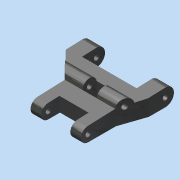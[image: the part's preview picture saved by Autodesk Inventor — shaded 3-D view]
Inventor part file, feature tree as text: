
AUTODESK INVENTOR PART (.ipt)
format: ipt  version: 2014 (Build 180170000, 170)  size: 160,256 bytes
history: native  units: in
note: dims shown in document units (in); Inventor stores cm internally (conversion verified against a paired STEP export)
features: other x3, plane x3, sketch x2
ambient origin geometry x8: Origin, YZ Plane, XZ Plane, XY Plane, X Axis, Y Axis, Z Axis, Center Point
bodies: Solid1 (feature_tree)
feature tree (8):
  other  "Shock Plate - Top (Right).ipt"
  other  "Solid1::Shock Plate - Top (Right).ipt"
  other  "TaggingFeature1"
  sketch  "Sketch3"  dims[d0=0.3937in]
  sketch  "Sketch5"  dims[d5=0.115in d8=1.8in d9=0.0in d21=1.28in d22=0.18in d24=0.0in d26=1.3in d27=0.23in d28=0.23in d29=0.4in d31=0.49in d32=0.31in d33=0.31in d34=0.4in d36=1.18in d37=0.63in]
  plane  "Work Plane1"
  plane  "Work Plane2"
  plane  "Work Plane3"
